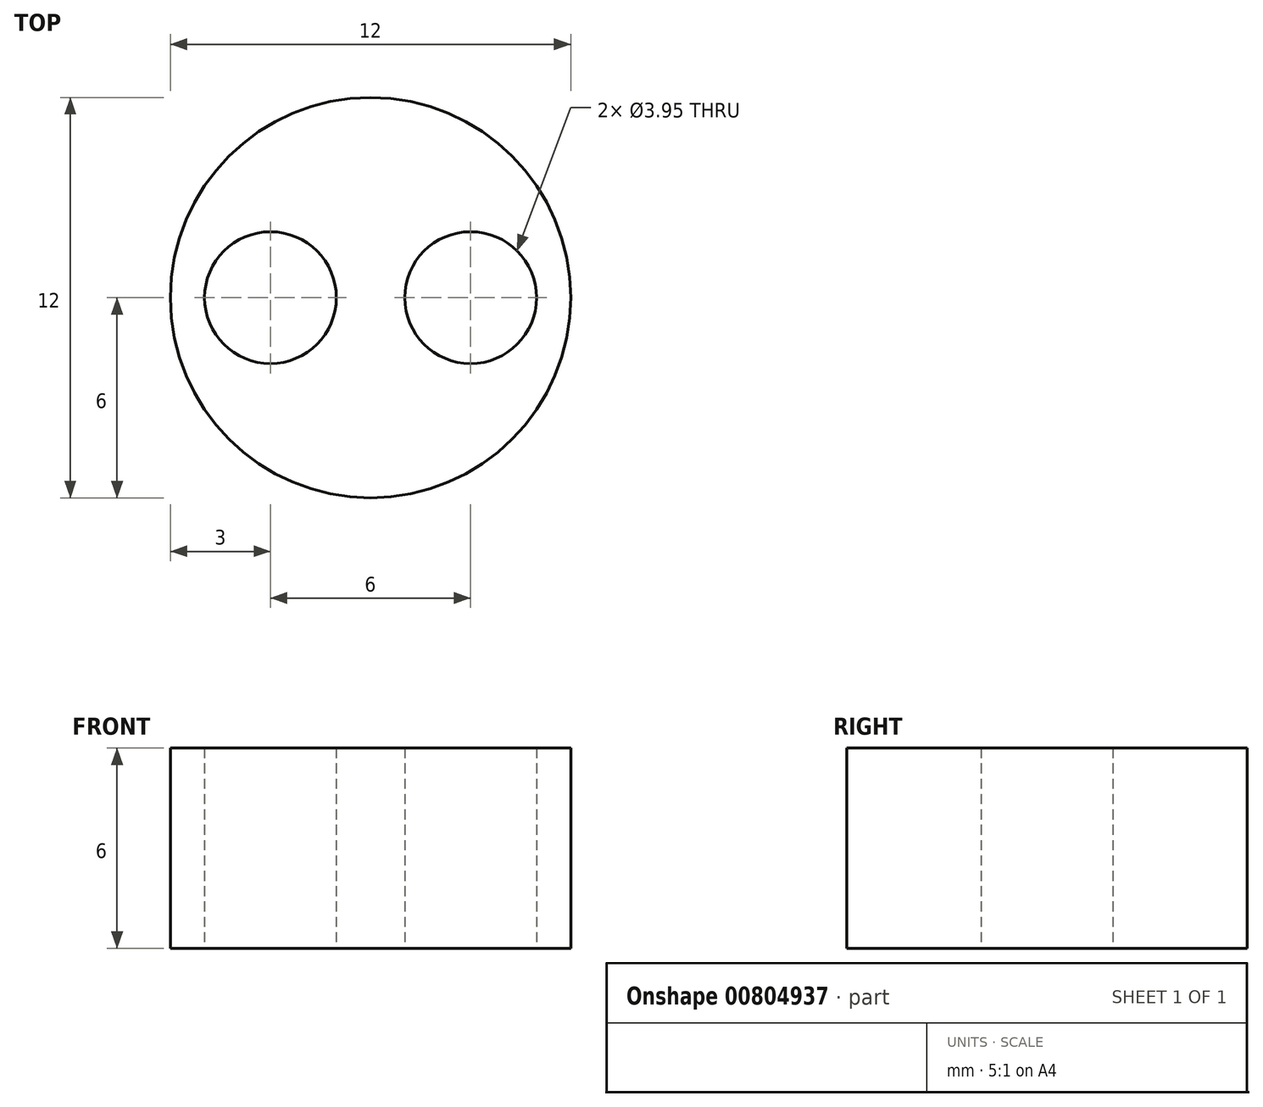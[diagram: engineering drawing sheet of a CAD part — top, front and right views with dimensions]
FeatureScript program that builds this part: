
annotation { "Feature Type Name" : "Feature", "Feature Type Description" : "" }
export const myFeature = defineFeature(function(context is Context, id is Id, definition is map)
    precondition{}
    {
        {
            var Q0;
            Q0=qCreatedBy(makeId("Top.planeOp"),FACE);
            var sketch = newSketch(context, id + "F0", { "sketchPlane" : qUnion([Q0])});
            skCircle(sketch, "E0", {"center": v(0, 0) * mm, "radius": 6 * mm});
            skCircle(sketch, "E1", {"center": v(-3, 0) * mm, "radius": 1.98 * mm});
            skCircle(sketch, "E2", {"center": v(3, 0) * mm, "radius": 1.98 * mm});
            skLineSegment(sketch, "E3", {"start": v(3, 0) * mm, "end": v(-3, 0) * mm, "construction": true});
            skSolve(sketch);
        }
        {
            var Q0;
            Q0 = qSketchRegion(id + "F0", true);
            extrude(context, id + "F1", {"entities" : qUnion([Q0]), "depth" : 6 * mm, "offsetDistance" : 25.4 * mm});
        }
    });
